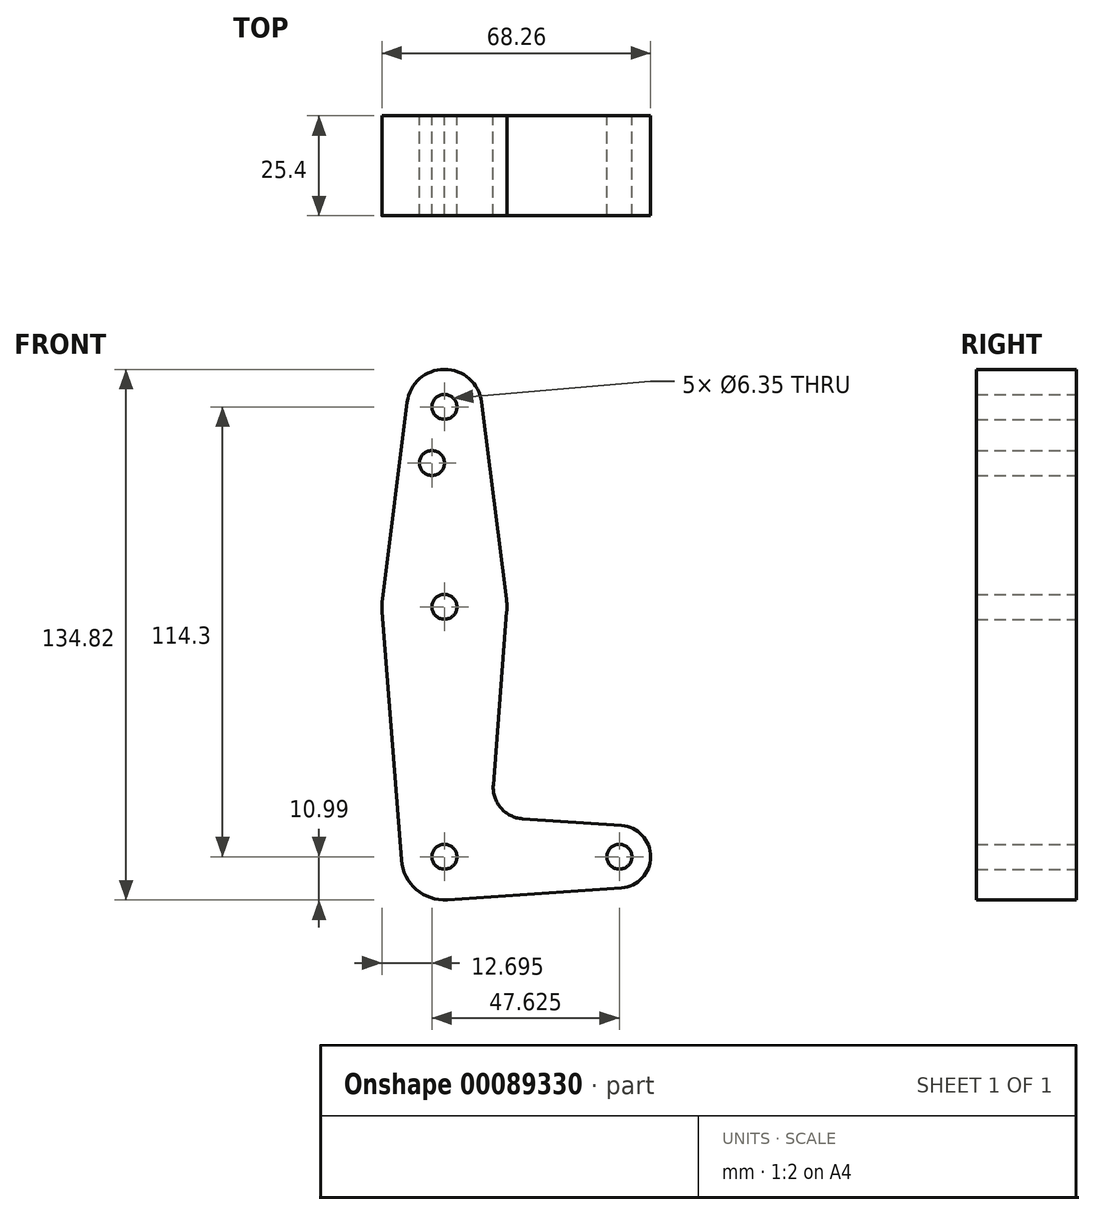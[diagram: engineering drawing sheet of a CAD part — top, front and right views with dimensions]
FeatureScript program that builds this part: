
annotation { "Feature Type Name" : "Feature", "Feature Type Description" : "" }
export const myFeature = defineFeature(function(context is Context, id is Id, definition is map)
    precondition{}
    {
        {
            var Q0;
            Q0=qCreatedBy(makeId("Front.planeOp"),FACE);
            var sketch = newSketch(context, id + "F0", { "sketchPlane" : qUnion([Q0])});
            skCircle(sketch, "E0", {"center": v(0, 0) * mm, "radius": 10.99 * mm});
            skCircle(sketch, "E1", {"center": v(44.45, 0) * mm, "radius": 7.94 * mm});
            skCircle(sketch, "E2", {"center": v(0, 63.5) * mm, "radius": 15.88 * mm});
            skCircle(sketch, "E3", {"center": v(0, 114.3) * mm, "radius": 9.53 * mm});
            skLineSegment(sketch, "E4", {"start": v(0, 0) * mm, "end": v(44.45, 0) * mm, "construction": true});
            skLineSegment(sketch, "E5", {"start": v(0, 0) * mm, "end": v(0, 114.3) * mm, "construction": true});
            skLineSegment(sketch, "E6", {"start": v(9.45, 115.5) * mm, "end": v(15.75, 65.48) * mm});
            skLineSegment(sketch, "E7", {"start": v(-9.45, 115.5) * mm, "end": v(-15.75, 65.48) * mm});
            skLineSegment(sketch, "E8", {"start": v(15.83, 62.28) * mm, "end": v(10.96, -0.85) * mm});
            skLineSegment(sketch, "E9", {"start": v(-15.83, 62.28) * mm, "end": v(-10.96, -0.85) * mm});
            skLineSegment(sketch, "E10", {"start": v(45, 7.92) * mm, "end": v(0.75, 10.96) * mm});
            skLineSegment(sketch, "E11", {"start": v(45, -7.92) * mm, "end": v(0.75, -10.96) * mm});
            skCircle(sketch, "E12", {"center": v(0, 114.3) * mm, "radius": 3.18 * mm});
            skCircle(sketch, "E13", {"center": v(0, 63.5) * mm, "radius": 3.18 * mm});
            skCircle(sketch, "E14", {"center": v(0, 0) * mm, "radius": 3.18 * mm});
            skCircle(sketch, "E15", {"center": v(44.45, 0) * mm, "radius": 3.18 * mm});
            skCircle(sketch, "E16", {"center": v(-3.18, 100.03) * mm, "radius": 3.18 * mm});
            skArc(sketch, "E17", {"start": v(12.43, 18.2) * mm, "mid": v(14.34, 12.39) * mm, "end": v(19.8, 9.65) * mm});
            skSolve(sketch);
        }
        {
            var Q0;
            Q0 = qSketchRegion(id + "F0", true);
            var Q1;
            {var subQ0=sQuery(id+"F0.wireOp",EDGE,"E8");var subQ1=sQuery(id+"F0.wireOp",EDGE,"E0");var subQ2=makeQuery(id+"F0.imprint","INTERSECT",VERTEX,{"derivedFrom":[subQ1,subQ0]});Q1=makeQuery(id+"F0.imprint","IMPRINT",FACE,{"disambiguationData":[TD([[makeQuery(id+"F0.imprint","IMPRINT",EDGE,{"disambiguationData":[TD([[subQ2,-1.0]])],"derivedFrom":subQ1}),-1.0]])]});}
            extrude(context, id + "F1", {"entities" : qUnion([Q0, Q1]), "depth" : 25.4 * mm});
        }
    });
